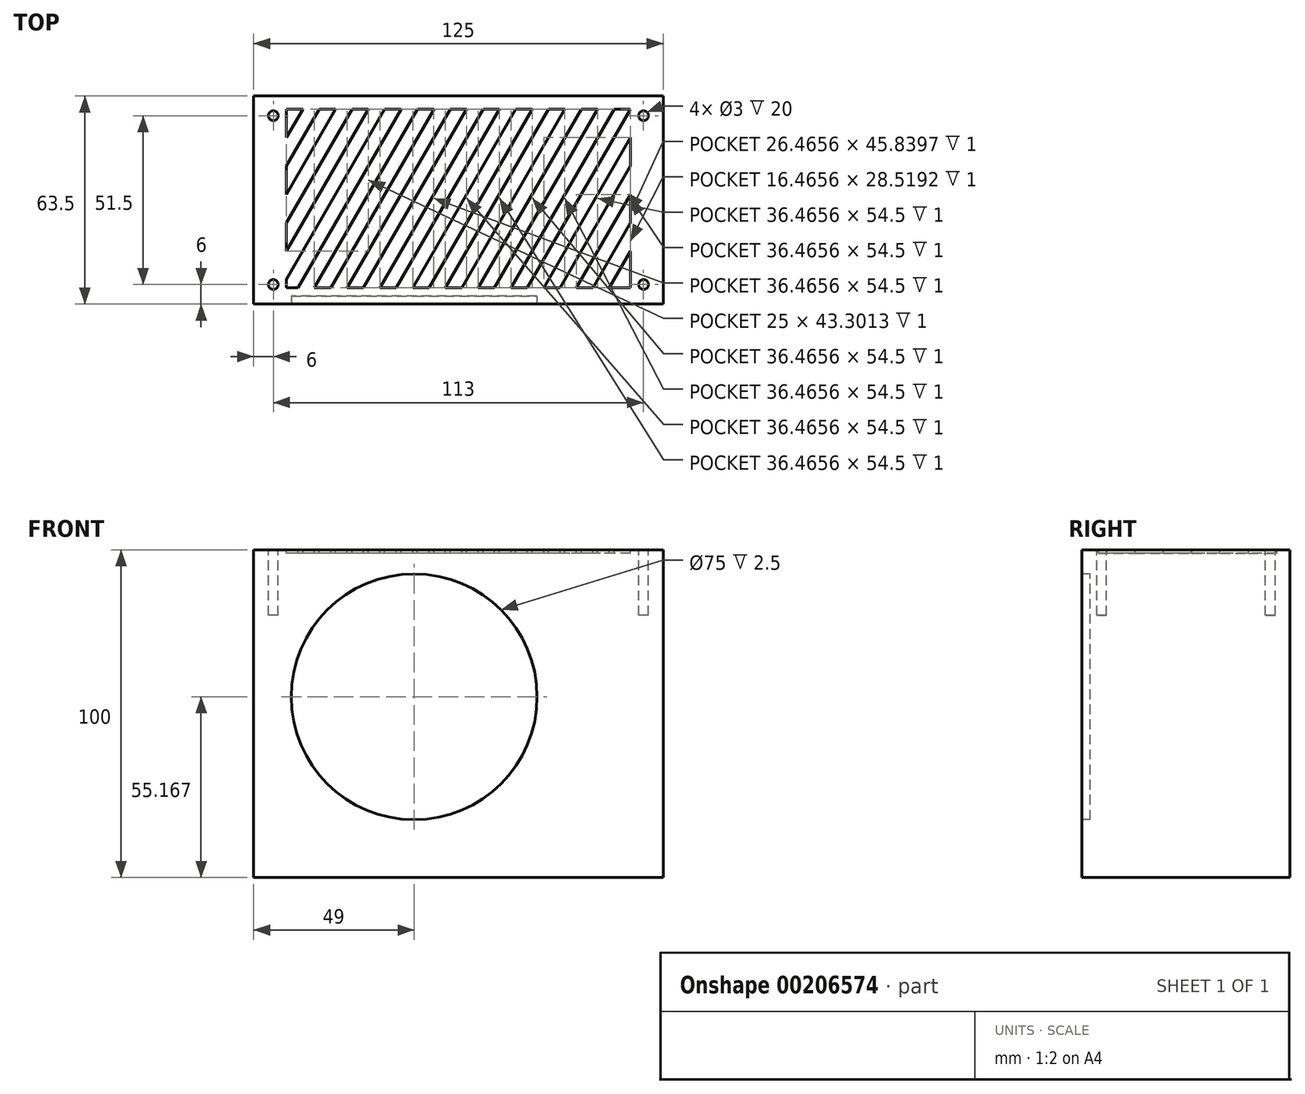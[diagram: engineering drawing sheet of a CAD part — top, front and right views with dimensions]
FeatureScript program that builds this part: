
annotation { "Feature Type Name" : "Feature", "Feature Type Description" : "" }
export const myFeature = defineFeature(function(context is Context, id is Id, definition is map)
    precondition{}
    {
        {
            var Q0;
            Q0=qCreatedBy(makeId("Front.planeOp"),FACE);
            var sketch = newSketch(context, id + "F0", { "sketchPlane" : qUnion([Q0])});
            skLineSegment(sketch, "E0.bottom", {"start": v(-62.5, 67.5) * mm, "end": v(62.5, 67.5) * mm});
            skLineSegment(sketch, "E0.top", {"start": v(-62.5, -32.5) * mm, "end": v(62.5, -32.5) * mm});
            skLineSegment(sketch, "E0.left", {"start": v(-62.5, 67.5) * mm, "end": v(-62.5, -32.5) * mm});
            skLineSegment(sketch, "E0.right", {"start": v(62.5, 67.5) * mm, "end": v(62.5, -32.5) * mm});
            skLineSegment(sketch, "E1.top", {"start": v(-62.5, -62.5) * mm, "end": v(62.5, -62.5) * mm});
            skLineSegment(sketch, "E1.left", {"start": v(-62.5, -32.5) * mm, "end": v(-62.5, -62.5) * mm});
            skLineSegment(sketch, "E1.right", {"start": v(62.5, -32.5) * mm, "end": v(62.5, -62.5) * mm});
            skSolve(sketch);
        }
        {
            var Q0;
            Q0=qCreatedBy(makeId("Front.planeOp"),FACE);
            var sketch = newSketch(context, id + "F1", { "sketchPlane" : qUnion([Q0])});
            skLineSegment(sketch, "E2.bottom", {"start": v(-53.5, 62.67) * mm, "end": v(26.5, 62.67) * mm});
            skLineSegment(sketch, "E2.top", {"start": v(-53.5, -17.33) * mm, "end": v(26.5, -17.33) * mm});
            skLineSegment(sketch, "E2.left", {"start": v(-53.5, 62.67) * mm, "end": v(-53.5, -17.33) * mm});
            skLineSegment(sketch, "E2.right", {"start": v(26.5, 62.67) * mm, "end": v(26.5, -17.33) * mm});
            skPoint(sketch, "E3", {"position": v(-13.5, 22.67) * mm});
            skCircle(sketch, "E4", {"center": v(-13.5, 22.67) * mm, "radius": 37.5 * mm});
            skSolve(sketch);
        }
        {
            var Q0;
            Q0=makeQuery(id+"F0.imprint","IMPRINT",FACE,{"disambiguationData":[TD([[makeQuery(id+"F0.imprint","IMPRINT",EDGE,{"derivedFrom":sQuery(id+"F0.wireOp",EDGE,"E0.bottom")}),-1.0]])]});
            extrude(context, id + "F2", {"entities" : qUnion([Q0]), "oppositeDirection" : true, "depth" : 63.5 * mm});
        }
        {
            var Q0;
            Q0=makeQuery(id+"F1.imprint","IMPRINT",FACE,{"disambiguationData":[TD([[makeQuery(id+"F1.imprint","IMPRINT",EDGE,{"derivedFrom":sQuery(id+"F1.wireOp",EDGE,"E4")}),1.0]])]});
            extrude(context, id + "F3", {"entities" : qUnion([Q0]), "operationType" : NewBodyOperationType.REMOVE, "endBound" : BoundingType.SYMMETRIC, "oppositeDirection" : true, "depth" : 5 * mm});
        }
        {
            var Q0;
            Q0=makeQuery(id+"F2.opExtrude","SWEPT_FACE",FACE,{"disambiguationData":[OSD([sQuery(id+"F0.wireOp",EDGE,"E0.bottom")])]});
            var sketch = newSketch(context, id + "F4", { "sketchPlane" : qUnion([Q0])});
            skLineSegment(sketch, "E5.bottom", {"start": v(52.5, 5) * mm, "end": v(-52.5, 5) * mm});
            skLineSegment(sketch, "E5.top", {"start": v(52.5, 59.5) * mm, "end": v(-52.5, 59.5) * mm});
            skLineSegment(sketch, "E5.left", {"start": v(52.5, 5) * mm, "end": v(52.5, 59.5) * mm});
            skLineSegment(sketch, "E5.right", {"start": v(-52.5, 5) * mm, "end": v(-52.5, 59.5) * mm});
            skPoint(sketch, "E5.middle", {"position": v(0, 32.25) * mm});
            skLineSegment(sketch, "E6", {"start": v(-52.5, 59.5) * mm, "end": v(-83.97, 5) * mm});
            skPoint(sketch, "E7", {"position": v(-68.23, 32.25) * mm});
            skLineSegment(sketch, "E8.1.0.0", {"start": v(-47.5, 59.5) * mm, "end": v(-78.97, 5) * mm});
            skLineSegment(sketch, "E8.2.0.0", {"start": v(-42.5, 59.5) * mm, "end": v(-73.97, 5) * mm});
            skLineSegment(sketch, "E8.3.0.0", {"start": v(-37.5, 59.5) * mm, "end": v(-68.97, 5) * mm});
            skLineSegment(sketch, "E8.4.0.0", {"start": v(-32.5, 59.5) * mm, "end": v(-63.97, 5) * mm});
            skLineSegment(sketch, "E8.5.0.0", {"start": v(-27.5, 59.5) * mm, "end": v(-58.97, 5) * mm});
            skLineSegment(sketch, "E8.6.0.0", {"start": v(-22.5, 59.5) * mm, "end": v(-53.97, 5) * mm});
            skLineSegment(sketch, "E8.7.0.0", {"start": v(-17.5, 59.5) * mm, "end": v(-48.97, 5) * mm});
            skLineSegment(sketch, "E8.8.0.0", {"start": v(-12.5, 59.5) * mm, "end": v(-43.97, 5) * mm});
            skLineSegment(sketch, "E8.9.0.0", {"start": v(-7.5, 59.5) * mm, "end": v(-38.97, 5) * mm});
            skLineSegment(sketch, "E8.10.0.0", {"start": v(-2.5, 59.5) * mm, "end": v(-33.97, 5) * mm});
            skLineSegment(sketch, "E8.11.0.0", {"start": v(2.5, 59.5) * mm, "end": v(-28.97, 5) * mm});
            skLineSegment(sketch, "E8.12.0.0", {"start": v(7.5, 59.5) * mm, "end": v(-23.97, 5) * mm});
            skLineSegment(sketch, "E8.13.0.0", {"start": v(12.5, 59.5) * mm, "end": v(-18.97, 5) * mm});
            skLineSegment(sketch, "E8.14.0.0", {"start": v(17.5, 59.5) * mm, "end": v(-13.97, 5) * mm});
            skLineSegment(sketch, "E8.15.0.0", {"start": v(22.5, 59.5) * mm, "end": v(-8.97, 5) * mm});
            skLineSegment(sketch, "E8.16.0.0", {"start": v(27.5, 59.5) * mm, "end": v(-3.97, 5) * mm});
            skLineSegment(sketch, "E8.17.0.0", {"start": v(32.5, 59.5) * mm, "end": v(1.03, 5) * mm});
            skLineSegment(sketch, "E8.18.0.0", {"start": v(37.5, 59.5) * mm, "end": v(6.03, 5) * mm});
            skLineSegment(sketch, "E8.19.0.0", {"start": v(42.5, 59.5) * mm, "end": v(11.03, 5) * mm});
            skLineSegment(sketch, "E8.20.0.0", {"start": v(47.5, 59.5) * mm, "end": v(16.03, 5) * mm});
            skLineSegment(sketch, "E8.21.0.0", {"start": v(52.5, 59.5) * mm, "end": v(21.03, 5) * mm});
            skLineSegment(sketch, "E8.22.0.0", {"start": v(57.5, 59.5) * mm, "end": v(26.03, 5) * mm});
            skLineSegment(sketch, "E8.23.0.0", {"start": v(62.5, 59.5) * mm, "end": v(31.03, 5) * mm});
            skLineSegment(sketch, "E8.24.0.0", {"start": v(67.5, 59.5) * mm, "end": v(36.03, 5) * mm});
            skLineSegment(sketch, "E8.25.0.0", {"start": v(72.5, 59.5) * mm, "end": v(41.03, 5) * mm});
            skLineSegment(sketch, "E8.26.0.0", {"start": v(77.5, 59.5) * mm, "end": v(46.03, 5) * mm});
            skLineSegment(sketch, "E8.27.0.0", {"start": v(82.5, 59.5) * mm, "end": v(51.03, 5) * mm});
            skLineSegment(sketch, "E8.28.0.0", {"start": v(87.5, 59.5) * mm, "end": v(56.03, 5) * mm});
            skLineSegment(sketch, "E8.29.0.0", {"start": v(92.5, 59.5) * mm, "end": v(61.03, 5) * mm});
            skLineSegment(sketch, "E8.direction1", {"start": v(-83.97, 5) * mm, "end": v(-78.97, 5) * mm, "construction": true});
            skSolve(sketch);
        }
        {
            var Q0;
            {var subQ1=sQuery(id+"F4.wireOp",EDGE,"E5.top");var subQ3=sQuery(id+"F4.wireOp",EDGE,"E8.1.0.0");var subQ4=makeQuery(id+"F4.imprint","INTERSECT",VERTEX,{"derivedFrom":[subQ1,subQ3]});Q0=makeQuery(id+"F4.imprint","IMPRINT",FACE,{"disambiguationData":[TD([[makeQuery(id+"F4.imprint","IMPRINT",EDGE,{"disambiguationData":[TD([[subQ4,-1.0]])],"derivedFrom":subQ3}),-1.0]])]});}
            var Q1;
            {var subQ0=sQuery(id+"F4.wireOp",EDGE,"E8.2.0.0");var subQ1=sQuery(id+"F4.wireOp",EDGE,"E5.top");var subQ2=makeQuery(id+"F4.imprint","INTERSECT",VERTEX,{"derivedFrom":[subQ1,subQ0]});Q1=makeQuery(id+"F4.imprint","IMPRINT",FACE,{"disambiguationData":[TD([[makeQuery(id+"F4.imprint","IMPRINT",EDGE,{"disambiguationData":[TD([[subQ2,1.0]])],"derivedFrom":subQ1}),1.0]])]});}
            var Q2;
            {var subQ0=sQuery(id+"F4.wireOp",EDGE,"E8.4.0.0");var subQ1=sQuery(id+"F4.wireOp",EDGE,"E5.top");var subQ2=makeQuery(id+"F4.imprint","INTERSECT",VERTEX,{"derivedFrom":[subQ1,subQ0]});Q2=makeQuery(id+"F4.imprint","IMPRINT",FACE,{"disambiguationData":[TD([[makeQuery(id+"F4.imprint","IMPRINT",EDGE,{"disambiguationData":[TD([[subQ2,1.0]])],"derivedFrom":subQ1}),1.0]])]});}
            var Q3;
            {var subQ7=sQuery(id+"F4.wireOp",EDGE,"E8.7.0.0");Q3=makeQuery(id+"F4.imprint","IMPRINT",FACE,{"disambiguationData":[TD([[makeQuery(id+"F4.imprint","IMPRINT",EDGE,{"derivedFrom":subQ7}),-1.0]])]});}
            var Q4;
            {var subQ0=sQuery(id+"F4.wireOp",EDGE,"E8.8.0.0");Q4=makeQuery(id+"F4.imprint","IMPRINT",FACE,{"disambiguationData":[TD([[makeQuery(id+"F4.imprint","IMPRINT",EDGE,{"derivedFrom":subQ0}),1.0]])]});}
            var Q5;
            {var subQ0=sQuery(id+"F4.wireOp",EDGE,"E8.10.0.0");Q5=makeQuery(id+"F4.imprint","IMPRINT",FACE,{"disambiguationData":[TD([[makeQuery(id+"F4.imprint","IMPRINT",EDGE,{"derivedFrom":subQ0}),1.0]])]});}
            var Q6;
            {var subQ0=sQuery(id+"F4.wireOp",EDGE,"E8.12.0.0");Q6=makeQuery(id+"F4.imprint","IMPRINT",FACE,{"disambiguationData":[TD([[makeQuery(id+"F4.imprint","IMPRINT",EDGE,{"derivedFrom":subQ0}),1.0]])]});}
            var Q7;
            {var subQ0=sQuery(id+"F4.wireOp",EDGE,"E8.14.0.0");Q7=makeQuery(id+"F4.imprint","IMPRINT",FACE,{"disambiguationData":[TD([[makeQuery(id+"F4.imprint","IMPRINT",EDGE,{"derivedFrom":subQ0}),1.0]])]});}
            var Q8;
            {var subQ0=sQuery(id+"F4.wireOp",EDGE,"E8.16.0.0");Q8=makeQuery(id+"F4.imprint","IMPRINT",FACE,{"disambiguationData":[TD([[makeQuery(id+"F4.imprint","IMPRINT",EDGE,{"derivedFrom":subQ0}),1.0]])]});}
            var Q9;
            {var subQ0=sQuery(id+"F4.wireOp",EDGE,"E8.18.0.0");Q9=makeQuery(id+"F4.imprint","IMPRINT",FACE,{"disambiguationData":[TD([[makeQuery(id+"F4.imprint","IMPRINT",EDGE,{"derivedFrom":subQ0}),1.0]])]});}
            var Q10;
            {var subQ0=sQuery(id+"F4.wireOp",EDGE,"E8.20.0.0");Q10=makeQuery(id+"F4.imprint","IMPRINT",FACE,{"disambiguationData":[TD([[makeQuery(id+"F4.imprint","IMPRINT",EDGE,{"derivedFrom":subQ0}),1.0]])]});}
            var Q11;
            {var subQ0=sQuery(id+"F4.wireOp",EDGE,"E8.22.0.0");Q11=makeQuery(id+"F4.imprint","IMPRINT",FACE,{"disambiguationData":[TD([[makeQuery(id+"F4.imprint","IMPRINT",EDGE,{"derivedFrom":subQ0}),1.0]])]});}
            var Q12;
            {var subQ0=sQuery(id+"F4.wireOp",EDGE,"E8.24.0.0");var subQ1=sQuery(id+"F4.wireOp",EDGE,"E5.bottom");var subQ2=makeQuery(id+"F4.imprint","INTERSECT",VERTEX,{"derivedFrom":[subQ1,subQ0]});Q12=makeQuery(id+"F4.imprint","IMPRINT",FACE,{"disambiguationData":[TD([[makeQuery(id+"F4.imprint","IMPRINT",EDGE,{"disambiguationData":[TD([[subQ2,1.0]])],"derivedFrom":subQ1}),-1.0]])]});}
            var Q13;
            {var subQ0=sQuery(id+"F4.wireOp",EDGE,"E8.26.0.0");var subQ1=sQuery(id+"F4.wireOp",EDGE,"E5.bottom");var subQ2=makeQuery(id+"F4.imprint","INTERSECT",VERTEX,{"derivedFrom":[subQ1,subQ0]});Q13=makeQuery(id+"F4.imprint","IMPRINT",FACE,{"disambiguationData":[TD([[makeQuery(id+"F4.imprint","IMPRINT",EDGE,{"disambiguationData":[TD([[subQ2,1.0]])],"derivedFrom":subQ1}),-1.0]])]});}
            var Q14;
            {var subQ0=sQuery(id+"F4.wireOp",EDGE,"E8.28.0.0");var subQ1=sQuery(id+"F4.wireOp",EDGE,"E5.bottom");var subQ2=makeQuery(id+"F4.imprint","INTERSECT",VERTEX,{"derivedFrom":[subQ1,subQ0]});Q14=makeQuery(id+"F4.imprint","IMPRINT",FACE,{"disambiguationData":[TD([[makeQuery(id+"F4.imprint","IMPRINT",EDGE,{"disambiguationData":[TD([[subQ2,1.0]])],"derivedFrom":subQ1}),-1.0]])]});}
            extrude(context, id + "F5", {"entities" : qUnion([Q0, Q1, Q2, Q3, Q4, Q5, Q6, Q7, Q8, Q9, Q10, Q11, Q12, Q13, Q14]), "operationType" : NewBodyOperationType.REMOVE, "oppositeDirection" : true, "depth" : 1 * mm});
        }
        {
            var Q0;
            Q0=makeQuery(id+"F2.opExtrude","SWEPT_FACE",FACE,{"disambiguationData":[OSD([sQuery(id+"F0.wireOp",EDGE,"E0.bottom")])]});
            var sketch = newSketch(context, id + "F6", { "sketchPlane" : qUnion([Q0])});
            skCircle(sketch, "E9", {"center": v(-56.5, 57.5) * mm, "radius": 1.5 * mm});
            skCircle(sketch, "E10", {"center": v(-56.5, 6) * mm, "radius": 1.5 * mm});
            skCircle(sketch, "E11", {"center": v(56.5, 57.5) * mm, "radius": 1.5 * mm});
            skCircle(sketch, "E12", {"center": v(56.5, 6) * mm, "radius": 1.5 * mm});
            skSolve(sketch);
        }
        {
            var Q0;
            Q0=makeQuery(id+"F6.imprint","IMPRINT",FACE,{"disambiguationData":[TD([[makeQuery(id+"F6.imprint","IMPRINT",EDGE,{"derivedFrom":sQuery(id+"F6.wireOp",EDGE,"E9")}),1.0]])]});
            var Q1;
            Q1=makeQuery(id+"F6.imprint","IMPRINT",FACE,{"disambiguationData":[TD([[makeQuery(id+"F6.imprint","IMPRINT",EDGE,{"derivedFrom":sQuery(id+"F6.wireOp",EDGE,"E11")}),1.0]])]});
            var Q2;
            Q2=makeQuery(id+"F6.imprint","IMPRINT",FACE,{"disambiguationData":[TD([[makeQuery(id+"F6.imprint","IMPRINT",EDGE,{"derivedFrom":sQuery(id+"F6.wireOp",EDGE,"E12")}),1.0]])]});
            var Q3;
            Q3=makeQuery(id+"F6.imprint","IMPRINT",FACE,{"disambiguationData":[TD([[makeQuery(id+"F6.imprint","IMPRINT",EDGE,{"derivedFrom":sQuery(id+"F6.wireOp",EDGE,"E10")}),1.0]])]});
            extrude(context, id + "F7", {"entities" : qUnion([Q0, Q1, Q2, Q3]), "operationType" : NewBodyOperationType.REMOVE, "oppositeDirection" : true, "depth" : 20 * mm});
        }
    });
